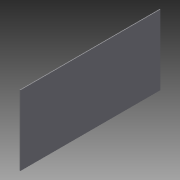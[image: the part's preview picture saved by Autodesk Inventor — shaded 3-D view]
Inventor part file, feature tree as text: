
AUTODESK INVENTOR PART (.ipt)
format: ipt  version: 2013 (Build 170138000, 138)  size: 72,192 bytes
history: native  units: in
note: dims shown in document units (in); Inventor stores cm internally (conversion verified against a paired STEP export)
features: sheet_metal_op x1, sketch x1, other x1
ambient origin geometry x8: Origin, YZ Plane, XZ Plane, XY Plane, X Axis, Y Axis, Z Axis, Center Point
bodies: Solid1 (feature_tree)
feature tree (3):
  sheet_metal_op  "Face1"
  sketch  "Sketch1"  dims[d0=12.0in d1=24.0in d2=0.12in]
  other  "Plate1"
